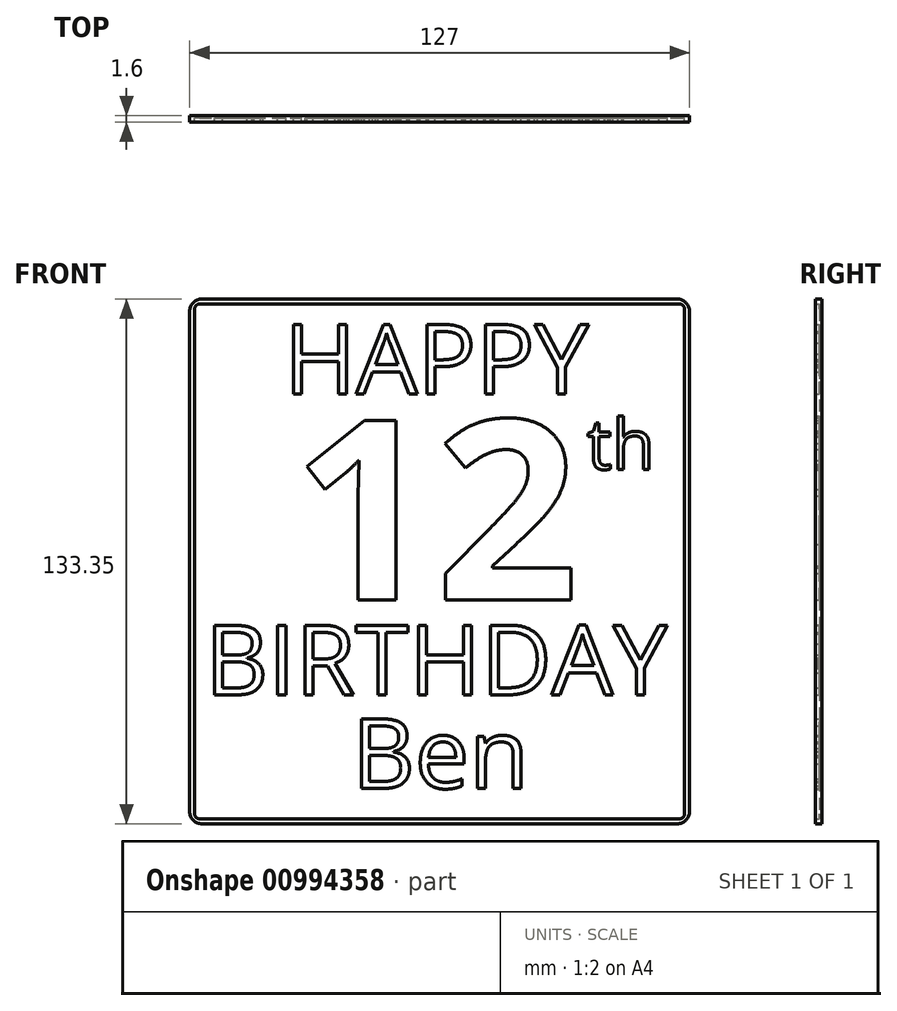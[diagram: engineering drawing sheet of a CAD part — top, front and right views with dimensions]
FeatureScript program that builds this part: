
annotation { "Feature Type Name" : "Feature", "Feature Type Description" : "" }
export const myFeature = defineFeature(function(context is Context, id is Id, definition is map)
    precondition{}
    {
        {
            var Q0;
            Q0=qCreatedBy(makeId("Front.planeOp"),FACE);
            var sketch = newSketch(context, id + "F0", { "sketchPlane" : qUnion([Q0])});
            skLineSegment(sketch, "E0.bottom", {"start": v(3.18, 0) * mm, "end": v(123.83, 0) * mm});
            skLineSegment(sketch, "E0.top", {"start": v(3.18, -133.35) * mm, "end": v(123.83, -133.35) * mm});
            skLineSegment(sketch, "E0.left", {"start": v(0, -3.17) * mm, "end": v(0, -130.18) * mm});
            skLineSegment(sketch, "E0.right", {"start": v(127, -3.17) * mm, "end": v(127, -130.18) * mm});
            skPoint(sketch, "E1.visualSharp", {"position": v(0, 0) * mm});
            skArc(sketch, "E1.filletArc", {"start": v(3.18, 0) * mm, "mid": v(0.93, -0.93) * mm, "end": v(0, -3.18) * mm});
            skPoint(sketch, "E2.visualSharp", {"position": v(127, 0) * mm});
            skArc(sketch, "E2.filletArc", {"start": v(127, -3.18) * mm, "mid": v(126.07, -0.93) * mm, "end": v(123.83, 0) * mm});
            skPoint(sketch, "E3.visualSharp", {"position": v(127, -133.35) * mm});
            skArc(sketch, "E3.filletArc", {"start": v(123.83, -133.35) * mm, "mid": v(126.07, -132.42) * mm, "end": v(127, -130.18) * mm});
            skPoint(sketch, "E4.visualSharp", {"position": v(0, -133.35) * mm});
            skArc(sketch, "E4.filletArc", {"start": v(0, -130.18) * mm, "mid": v(0.93, -132.42) * mm, "end": v(3.18, -133.35) * mm});
            skSolve(sketch);
        }
        {
            var Q0;
            Q0=qSketchRegion(id+"F0",true);
            extrude(context, id + "F1", {"entities" : qUnion([Q0]), "depth" : .6 * mm, "offsetDistance" : 25.4 * mm});
        }
        {
            var Q0;
            Q0=makeQuery(id+"F1.opExtrude","CAP_FACE",FACE,{"disambiguationData":[OSD([sQuery(id+"F0.wireOp",EDGE,"E0.bottom"),sQuery(id+"F0.wireOp",EDGE,"E0.top"),sQuery(id+"F0.wireOp",EDGE,"E0.left"),sQuery(id+"F0.wireOp",EDGE,"E0.right"),sQuery(id+"F0.wireOp",EDGE,"E1.filletArc"),sQuery(id+"F0.wireOp",EDGE,"E2.filletArc"),sQuery(id+"F0.wireOp",EDGE,"E3.filletArc"),sQuery(id+"F0.wireOp",EDGE,"E4.filletArc")])],"isStart":false});
            var sketch = newSketch(context, id + "F2", { "sketchPlane" : qUnion([Q0])});
            skText(sketch, "E5", { "text": "HAPPY", "fontName": "OpenSans-Regular.ttf"});
            skText(sketch, "E6", { "text": "BIRTHDAY", "fontName": "OpenSans-Regular.ttf"});
            skText(sketch, "E7", { "text": "12", "fontName": "OpenSans-Bold.ttf"});
            skText(sketch, "E8", { "text": "th", "fontName": "OpenSans-Regular.ttf"});
            skText(sketch, "E9", { "text": "Ben", "fontName": "OpenSans-Regular.ttf"});
            skLineSegment(sketch, "E10", {"start": v(63.5, 0) * mm, "end": v(63.5, -6.35) * mm, "construction": true});
            skLineSegment(sketch, "E11", {"start": v(63.5, -24.13) * mm, "end": v(63.5, -30.48) * mm, "construction": true});
            skLineSegment(sketch, "E12", {"start": v(63.5, -76.4) * mm, "end": v(63.5, -82.76) * mm, "construction": true});
            skLineSegment(sketch, "E13", {"start": v(63.5, -100.54) * mm, "end": v(63.5, -106.53) * mm, "construction": true});
            skLineSegment(sketch, "E14", {"start": v(63.5, -124.3) * mm, "end": v(63.5, -129.53) * mm, "construction": true});
            skLineSegment(sketch, "E15", {"start": v(63.5, -147.31) * mm, "end": v(63.5, -133.35) * mm, "construction": true});
            const initialGuessF2  = {"E5": [0.024, -0.02413, 1, 0, 0.01778], "E6": [0.00395, -0.10054, 1, 0, 0.01778], "E7": [0.02603, -0.0764, 1, 0, 0.04593], "E8": [0.10097, -0.04326, 1, 0, 0.01278], "E9": [0.04119, -0.1243, 1, 0, 0.01778]};
            skSetInitialGuess(sketch, initialGuessF2);
            skSolve(sketch);
        }
        {
            var Q0;
            Q0=qSketchRegion(id+"F2",true);
            extrude(context, id + "F3", {"entities" : qUnion([Q0]), "operationType" : NewBodyOperationType.ADD, "depth" : 1 * mm, "offsetDistance" : 25.4 * mm});
        }
        {
            var Q0;
            {var subQ0=sQuery(id+"F0.wireOp",EDGE,"E2.filletArc");var subQ1=sQuery(id+"F0.wireOp",EDGE,"E0.bottom");var subQ2=sQuery(id+"F0.wireOp",EDGE,"E0.top");var subQ3=sQuery(id+"F0.wireOp",EDGE,"E0.left");var subQ4=sQuery(id+"F0.wireOp",EDGE,"E0.right");var subQ5=sQuery(id+"F0.wireOp",EDGE,"E1.filletArc");var subQ6=sQuery(id+"F0.wireOp",EDGE,"E3.filletArc");var subQ7=sQuery(id+"F0.wireOp",EDGE,"E4.filletArc");Q0=makeQuery(id+"F3.boolean.opBoolean","SPLIT",FACE,{"disambiguationData":[TD([makeQuery(id+"F1.opExtrude","SWEPT_FACE",FACE,{"disambiguationData":[OSD([subQ1])]})])],"derivedFrom":makeQuery(id+"F1.opExtrude","CAP_FACE",FACE,{"disambiguationData":[OSD([subQ1,subQ2,subQ3,subQ4,subQ5,subQ0,subQ6,subQ7])],"isStart":false})});}
            var sketch = newSketch(context, id + "F4", { "sketchPlane" : qUnion([Q0])});
            skLineSegment(sketch, "E16.0", {"start": v(127, -3.17) * mm, "end": v(127, -130.18) * mm});
            skLineSegment(sketch, "E16.1", {"start": v(3.18, -133.35) * mm, "end": v(123.83, -133.35) * mm});
            skLineSegment(sketch, "E16.2", {"start": v(0, -3.17) * mm, "end": v(0, -130.18) * mm});
            skLineSegment(sketch, "E16.3", {"start": v(3.17, 0) * mm, "end": v(123.83, 0) * mm});
            skArc(sketch, "E16.4", {"start": v(127, -3.18) * mm, "mid": v(126.07, -0.93) * mm, "end": v(123.83, 0) * mm});
            skArc(sketch, "E16.5", {"start": v(123.83, -133.35) * mm, "mid": v(126.07, -132.42) * mm, "end": v(127, -130.18) * mm});
            skArc(sketch, "E16.6", {"start": v(0, -130.18) * mm, "mid": v(0.93, -132.42) * mm, "end": v(3.18, -133.35) * mm});
            skArc(sketch, "E16.7", {"start": v(3.18, 0) * mm, "mid": v(0.93, -0.93) * mm, "end": v(0, -3.18) * mm});
            skLineSegment(sketch, "E17.0", {"start": v(2.54, -1.27) * mm, "end": v(124.46, -1.27) * mm});
            skLineSegment(sketch, "E17.1", {"start": v(1.27, -2.54) * mm, "end": v(1.27, -130.81) * mm});
            skLineSegment(sketch, "E17.2", {"start": v(2.54, -132.08) * mm, "end": v(124.46, -132.08) * mm});
            skLineSegment(sketch, "E17.3", {"start": v(125.73, -2.54) * mm, "end": v(125.73, -130.81) * mm});
            skPoint(sketch, "E18.visualSharp", {"position": v(125.73, -132.08) * mm});
            skArc(sketch, "E18.filletArc", {"start": v(124.46, -132.08) * mm, "mid": v(125.36, -131.7) * mm, "end": v(125.73, -130.81) * mm});
            skPoint(sketch, "E19.visualSharp", {"position": v(125.73, -1.27) * mm});
            skArc(sketch, "E19.filletArc", {"start": v(125.73, -2.54) * mm, "mid": v(125.36, -1.64) * mm, "end": v(124.46, -1.27) * mm});
            skPoint(sketch, "E20.visualSharp", {"position": v(1.27, -132.08) * mm});
            skArc(sketch, "E20.filletArc", {"start": v(1.27, -130.81) * mm, "mid": v(1.64, -131.7) * mm, "end": v(2.54, -132.08) * mm});
            skPoint(sketch, "E21.visualSharp", {"position": v(1.27, -1.27) * mm});
            skArc(sketch, "E21.filletArc", {"start": v(2.54, -1.27) * mm, "mid": v(1.64, -1.64) * mm, "end": v(1.27, -2.54) * mm});
            skSolve(sketch);
        }
        {
            var Q0;
            Q0=qSketchRegion(id+"F4",true);
            extrude(context, id + "F5", {"entities" : qUnion([Q0]), "operationType" : NewBodyOperationType.ADD, "depth" : 1 * mm, "offsetDistance" : 25.4 * mm});
        }
    });
